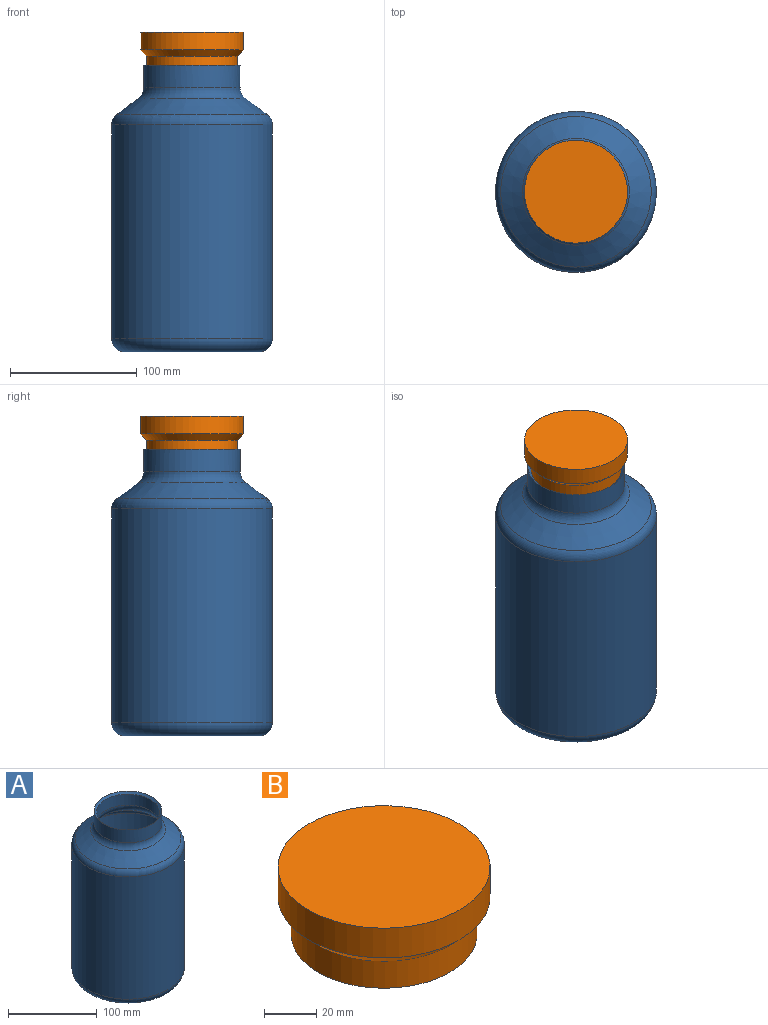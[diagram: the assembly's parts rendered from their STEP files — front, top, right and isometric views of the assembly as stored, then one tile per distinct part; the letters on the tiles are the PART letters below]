
ASSEMBLY  parts=2 mates=1
PART A: 15 faces, bbox 137.5x137.5x226.1 mm
  f0: plane 106.68x106.68mm, normal (0,0,-1), area 8938.3mm2, adj f6
  f1: cylinder r=38.1mm len=76.2mm, axis (0,0,-1), area 4256.3mm2, adj f4,f14
  f2: cone r=38.1mm half-angle=53.1deg, axis (0,0,-1), area 6891.2mm2, adj f4,f5
  f3: cylinder r=63.5mm len=168.91mm, axis (0,0,-1), area 67392.1mm2, adj f5,f6
  f4: torus R=48.26mm, axis (0,0,-1), area 2337.9mm2, adj f1,f2
  f5: torus R=53.34mm, axis (0,0,1), area 3676.4mm2, adj f2,f3
  f6: torus R=53.34mm, axis (0,0,1), area 5997.3mm2, adj f0,f3
  f7: plane 106.68x106.68mm, normal (0,0,1), area 8938.3mm2, adj f13
  f8: cylinder r=35.56mm len=71.12mm, axis (0,0,-1), area 3405.1mm2, adj f11,f14
  f9: cone r=36.58mm half-angle=53.1deg, axis (0,0,-1), area 6684.5mm2, adj f11,f12
  f10: cylinder r=60.96mm len=168.91mm, axis (0,0,-1), area 64696.4mm2, adj f12,f13
  f11: torus R=48.26mm, axis (0,0,-1), area 2760.3mm2, adj f8,f9
  f12: torus R=53.34mm, axis (0,0,1), area 2660mm2, adj f9,f10
  f13: torus R=53.34mm, axis (0,0,1), area 4376.3mm2, adj f7,f10
  f14: cone r=40.64mm half-angle=45deg, axis (0,0,1), area 831.2mm2, adj f1,f8
PART B: 5 faces, bbox 81.3x81.3x31.8 mm
  f0: plane 71.12x71.12mm, normal (0,0,-1), area 3972.6mm2, adj f3
  f1: plane 81.28x81.28mm, normal (0,0,1), area 5188.7mm2, adj f2
  f2: cylinder r=40.64mm len=81.28mm, axis (0,0,1), area 3567.2mm2, adj f1,f4
  f3: cylinder r=35.56mm len=71.12mm, axis (0,0,1), area 2837.6mm2, adj f0,f4
  f4: cone r=40.64mm half-angle=45deg, axis (0,0,1), area 1719.8mm2, adj f2,f3
PLACE A t=(-12.22,52.33,-34.94)mm
PLACE B t=(-12.22,52.33,185.6)mm
MATE cylindrical B.f2 <-> A.f1  axis (0,0,1) through (-12.22,52.33,191.95)mm
